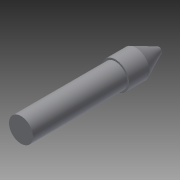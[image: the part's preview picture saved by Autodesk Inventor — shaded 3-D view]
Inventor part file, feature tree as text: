
AUTODESK INVENTOR PART (.ipt)
format: ipt  version: 2013 (Build 170138000, 138)  size: 82,944 bytes
history: native  units: mm
features: revolve x1, sketch x1
ambient origin geometry x8: Origin, YZ Plane, XZ Plane, XY Plane, X Axis, Y Axis, Z Axis, Center Point
bodies: Solid1 (feature_tree)
feature tree (2):
  revolve  "Revolution1"  [1 undecoded]
  sketch  "Sketch1"  dims[d0=8.25mm d1=65.0mm d2=1.25mm d3=14.0mm d4=95.0mm d5=2.0mm d6=90.0deg]
note: 1 required parameter value undecoded (feature->parameter linkage not recoverable at this tier; creation-order binding heuristic only, values carry confidence <= 0.55)
